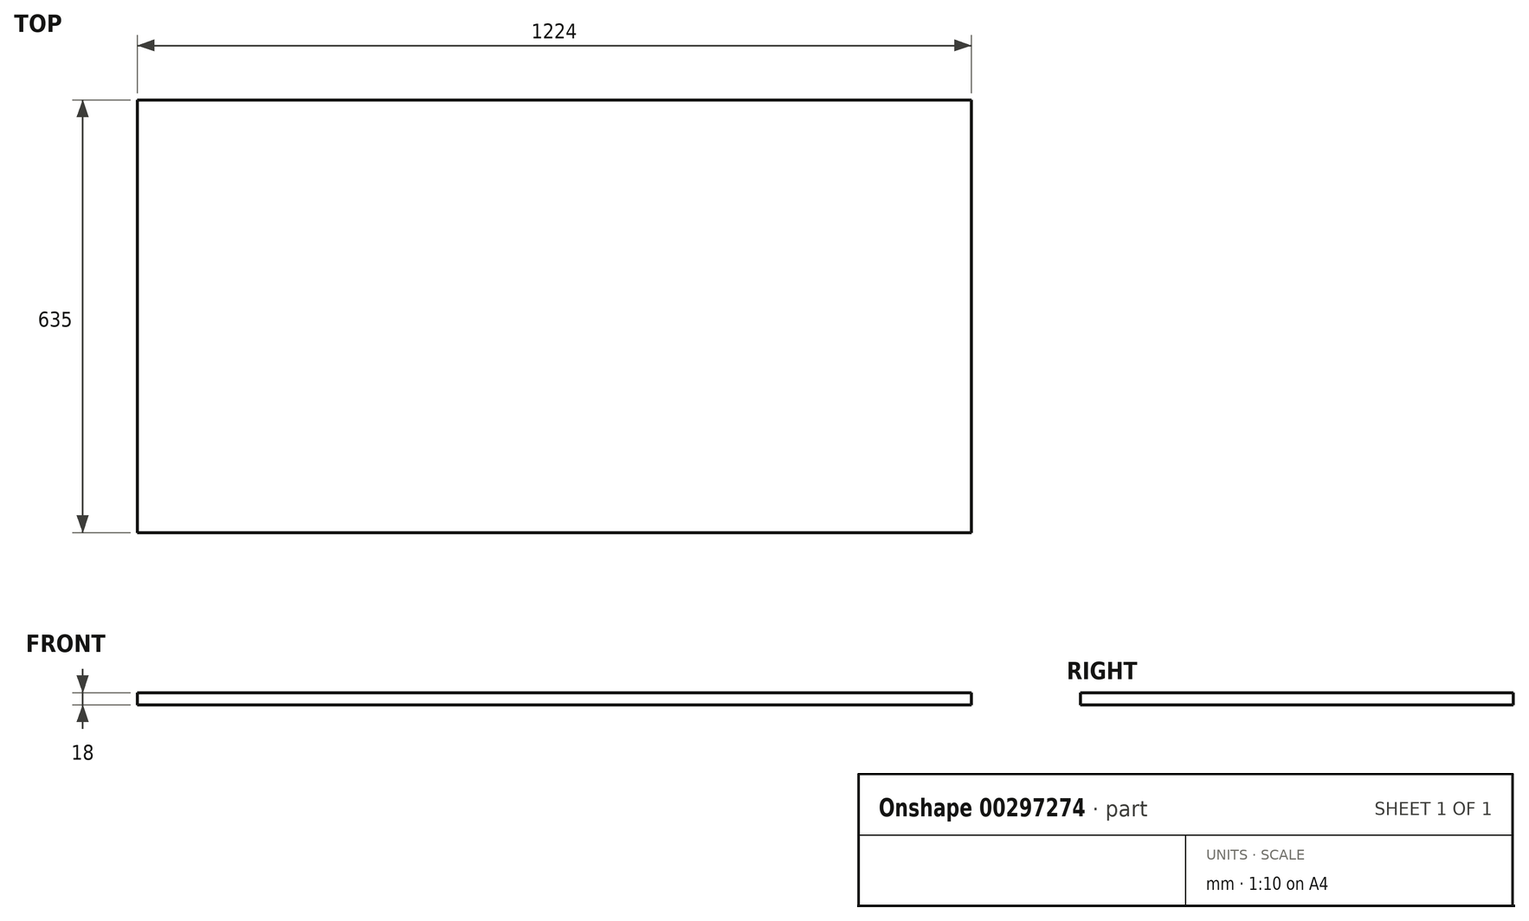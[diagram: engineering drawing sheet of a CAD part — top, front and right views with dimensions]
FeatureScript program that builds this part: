
annotation { "Feature Type Name" : "Feature", "Feature Type Description" : "" }
export const myFeature = defineFeature(function(context is Context, id is Id, definition is map)
    precondition{}
    {
        {
            var Q0;
            Q0=qCreatedBy(makeId("Top.planeOp"),FACE);
            var sketch = newSketch(context, id + "F0", { "sketchPlane" : qUnion([Q0])});
            skLineSegment(sketch, "E0.bottom", {"start": v(612, -317.5) * mm, "end": v(-612, -317.5) * mm});
            skLineSegment(sketch, "E0.top", {"start": v(612, 317.5) * mm, "end": v(-612, 317.5) * mm});
            skLineSegment(sketch, "E0.left", {"start": v(612, -317.5) * mm, "end": v(612, 317.5) * mm});
            skLineSegment(sketch, "E0.right", {"start": v(-612, -317.5) * mm, "end": v(-612, 317.5) * mm});
            skPoint(sketch, "E0.middle", {"position": v(0, 0) * mm});
            skSolve(sketch);
        }
        {
            var Q0;
            Q0=qSketchRegion(id+"F0",true);
            extrude(context, id + "F1", {"entities" : qUnion([Q0]), "depth" : 18 * mm});
        }
    });
